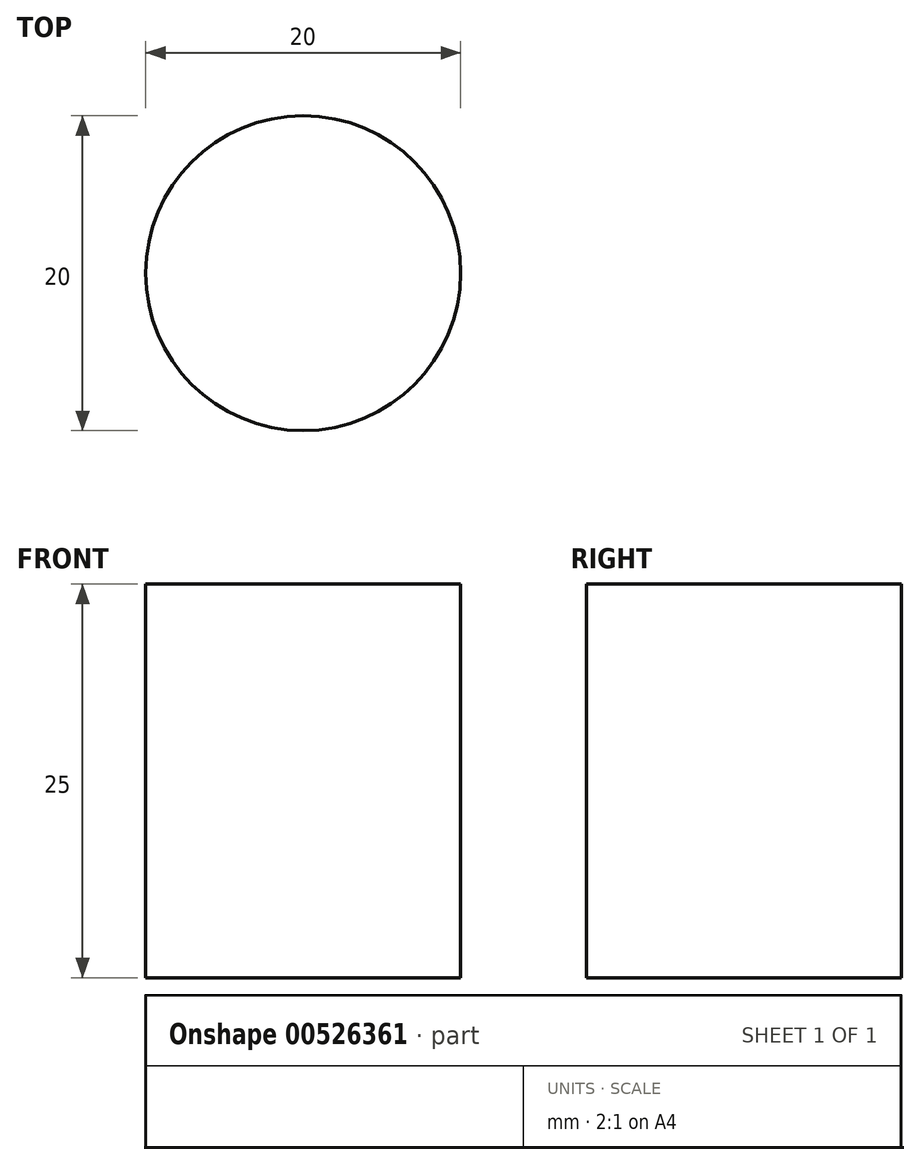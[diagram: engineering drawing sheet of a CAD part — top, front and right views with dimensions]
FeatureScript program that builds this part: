
annotation { "Feature Type Name" : "Feature", "Feature Type Description" : "" }
export const myFeature = defineFeature(function(context is Context, id is Id, definition is map)
    precondition{}
    {
        {
            var Q0;
            Q0=qCreatedBy(makeId("Top.planeOp"),FACE);
            var sketch = newSketch(context, id + "F0", { "sketchPlane" : qUnion([Q0])});
            skCircle(sketch, "E0", {"center": v(0, 0) * mm, "radius": 10 * mm});
            skSolve(sketch);
        }
        {
            var Q0;
            Q0 = qSketchRegion(id + "F0", true);
            extrude(context, id + "F1", {"entities" : qUnion([Q0]), "depth" : 25 * mm, "offsetDistance" : 25 * mm});
        }
    });
